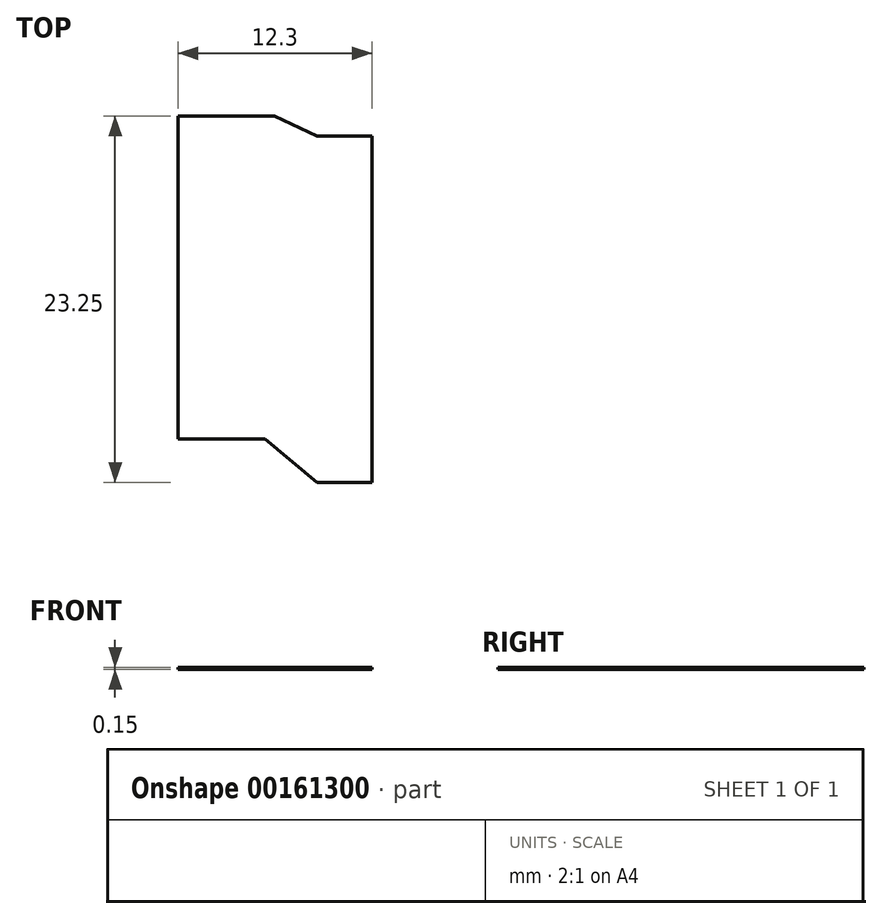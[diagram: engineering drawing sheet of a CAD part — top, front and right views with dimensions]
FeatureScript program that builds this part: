
annotation { "Feature Type Name" : "Feature", "Feature Type Description" : "" }
export const myFeature = defineFeature(function(context is Context, id is Id, definition is map)
    precondition{}
    {
        {
            var Q0;
            Q0=qCreatedBy(makeId("Top.planeOp"),FACE);
            var sketch = newSketch(context, id + "F0", { "sketchPlane" : qUnion([Q0])});
            skLineSegment(sketch, "E0", {"start": v(-7.95, 5.58) * mm, "end": v(-7.95, -14.92) * mm});
            skLineSegment(sketch, "E1", {"start": v(-7.95, -14.92) * mm, "end": v(-2.43, -14.92) * mm});
            skLineSegment(sketch, "E2", {"start": v(-2.43, -14.92) * mm, "end": v(0.85, -17.67) * mm});
            skLineSegment(sketch, "E3", {"start": v(0.85, -17.67) * mm, "end": v(4.35, -17.67) * mm});
            skLineSegment(sketch, "E4", {"start": v(4.35, -17.67) * mm, "end": v(4.35, 4.33) * mm});
            skLineSegment(sketch, "E5", {"start": v(4.35, 4.33) * mm, "end": v(0.85, 4.33) * mm});
            skLineSegment(sketch, "E6", {"start": v(0.85, 4.33) * mm, "end": v(-1.83, 5.58) * mm});
            skLineSegment(sketch, "E7", {"start": v(-1.83, 5.58) * mm, "end": v(-7.95, 5.58) * mm});
            skSolve(sketch);
        }
        {
            var Q0;
            Q0 = qSketchRegion(id + "F0", true);
            extrude(context, id + "F1", {"entities" : qUnion([Q0]), "depth" : 0.15 * mm});
        }
    });
